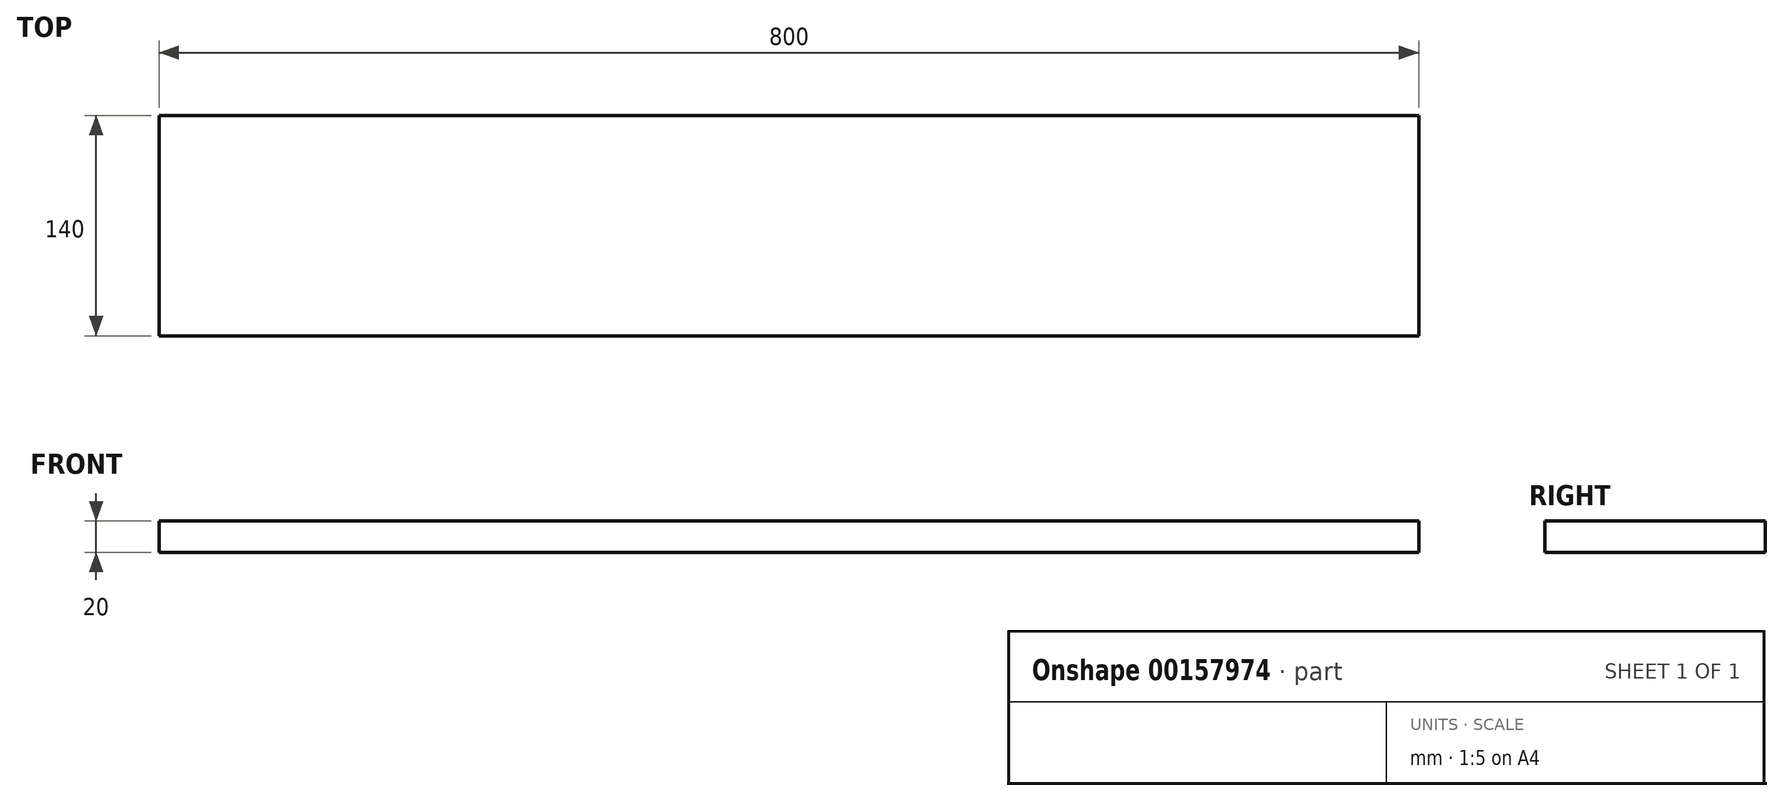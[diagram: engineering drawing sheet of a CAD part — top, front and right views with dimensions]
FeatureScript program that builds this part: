
annotation { "Feature Type Name" : "Feature", "Feature Type Description" : "" }
export const myFeature = defineFeature(function(context is Context, id is Id, definition is map)
    precondition{}
    {
        {
            var Q0;
            Q0=qCreatedBy(makeId("Top.planeOp"),FACE);
            var sketch = newSketch(context, id + "F0", { "sketchPlane" : qUnion([Q0])});
            skLineSegment(sketch, "E0.bottom", {"start": v(-400, -70) * mm, "end": v(400, -70) * mm});
            skLineSegment(sketch, "E0.top", {"start": v(-400, 70) * mm, "end": v(400, 70) * mm});
            skLineSegment(sketch, "E0.left", {"start": v(-400, -70) * mm, "end": v(-400, 70) * mm});
            skLineSegment(sketch, "E0.right", {"start": v(400, -70) * mm, "end": v(400, 70) * mm});
            skPoint(sketch, "E0.middle", {"position": v(0, 0) * mm});
            skSolve(sketch);
        }
        {
            var Q0;
            Q0=qSketchRegion(id+"F0",true);
            extrude(context, id + "F1", {"entities" : qUnion([Q0]), "endBound" : BoundingType.SYMMETRIC, "depth" : 20 * mm});
        }
    });
